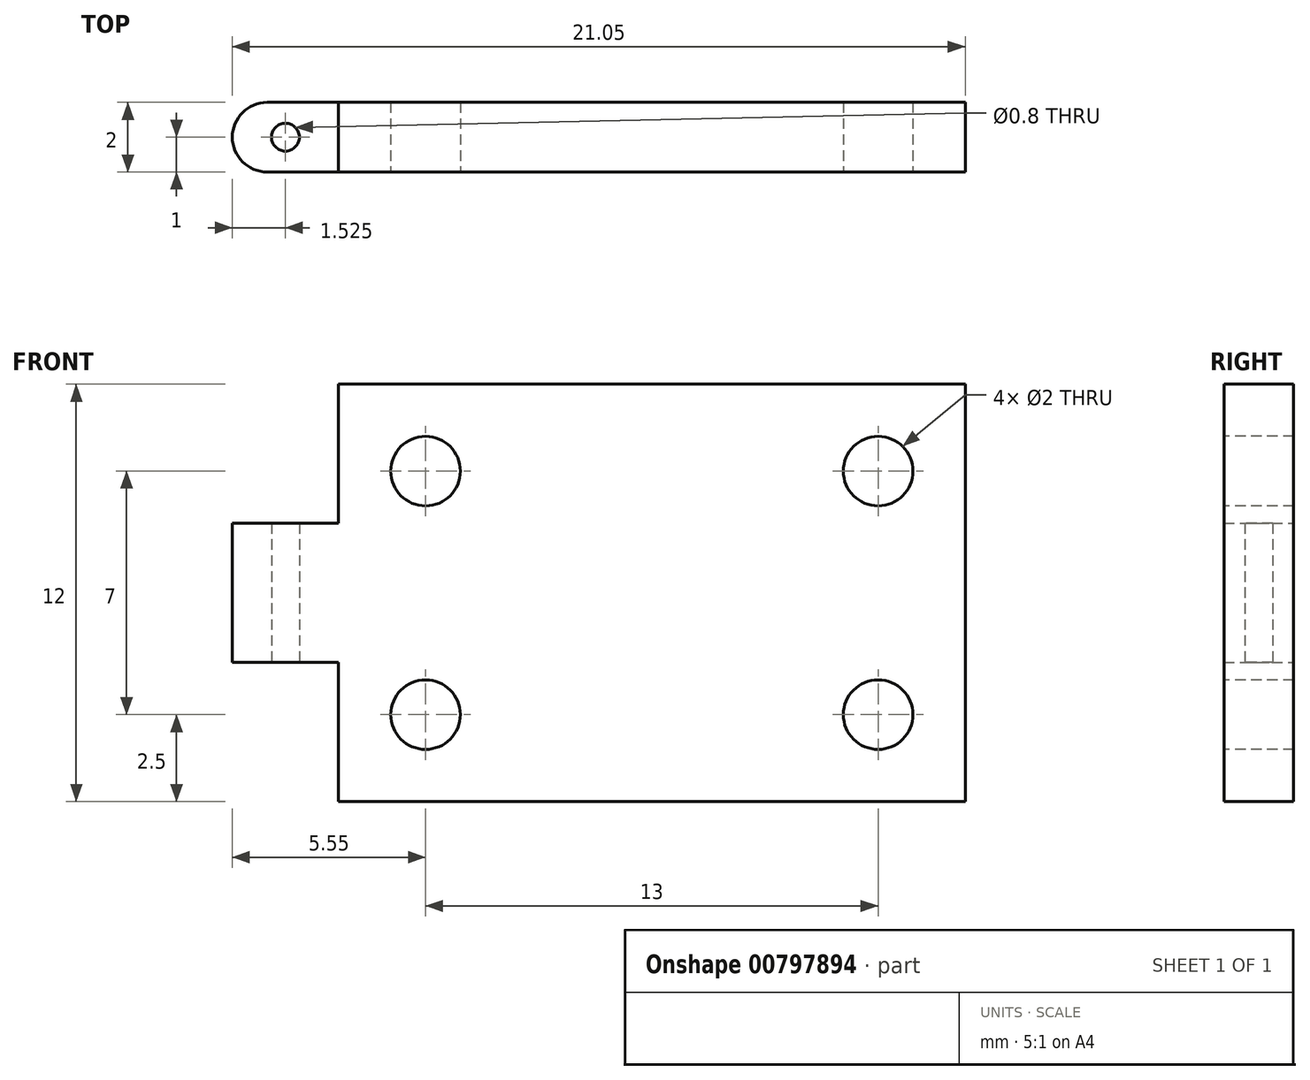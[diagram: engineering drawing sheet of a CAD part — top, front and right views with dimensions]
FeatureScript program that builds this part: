
annotation { "Feature Type Name" : "Feature", "Feature Type Description" : "" }
export const myFeature = defineFeature(function(context is Context, id is Id, definition is map)
    precondition{}
    {
        {
            var Q0;
            Q0=qCreatedBy(makeId("Front.planeOp"),FACE);
            var sketch = newSketch(context, id + "F0", { "sketchPlane" : qUnion([Q0])});
            skLineSegment(sketch, "E0.bottom", {"start": v(9, 6) * mm, "end": v(-9, 6) * mm});
            skLineSegment(sketch, "E0.top", {"start": v(9, -6) * mm, "end": v(-9, -6) * mm});
            skLineSegment(sketch, "E0.left", {"start": v(9, 6) * mm, "end": v(9, -6) * mm});
            skLineSegment(sketch, "E0.right", {"start": v(-9, 6) * mm, "end": v(-9, -6) * mm});
            skPoint(sketch, "E0.middle", {"position": v(0, 0) * mm});
            skLineSegment(sketch, "E1.bottom", {"start": v(-5.95, 2) * mm, "end": v(-12.05, 2) * mm});
            skLineSegment(sketch, "E1.top", {"start": v(-5.95, -2) * mm, "end": v(-12.05, -2) * mm});
            skLineSegment(sketch, "E1.left", {"start": v(-5.95, 2) * mm, "end": v(-5.95, -2) * mm});
            skLineSegment(sketch, "E1.right", {"start": v(-12.05, 2) * mm, "end": v(-12.05, -2) * mm});
            skPoint(sketch, "E1.middle", {"position": v(-9, 0) * mm});
            skSolve(sketch);
        }
        {
            var Q0;
            Q0 = qSketchRegion(id + "F0", true);
            extrude(context, id + "F1", {"entities" : qUnion([Q0]), "depth" : 2 * mm, "offsetDistance" : 25 * mm});
        }
        {
            var Q0;
            Q0=makeQuery(id+"F1.opExtrude","SWEPT_FACE",FACE,{"disambiguationData":[OSD([sQuery(id+"F0.wireOp",EDGE,"E1.top")])]});
            var sketch = newSketch(context, id + "F2", { "sketchPlane" : qUnion([Q0])});
            skLineSegment(sketch, "E2", {"start": v(-12.05, 2) * mm, "end": v(-9, 0) * mm, "construction": true});
            skCircle(sketch, "E3", {"center": v(-10.53, 1) * mm, "radius": 0.4 * mm});
            skSolve(sketch);
        }
        {
            var Q0;
            Q0 = qSketchRegion(id + "F2", true);
            extrude(context, id + "F3", {"entities" : qUnion([Q0]), "operationType" : NewBodyOperationType.REMOVE, "oppositeDirection" : true, "depth" : 25 * mm, "offsetDistance" : 25 * mm});
        }
        {
            var Q0;
            Q0=makeQuery(id+"F1.opExtrude","CAP_FACE",FACE,{"disambiguationData":[OSD([sQuery(id+"F0.wireOp",EDGE,"E0.bottom"),sQuery(id+"F0.wireOp",EDGE,"E0.top"),sQuery(id+"F0.wireOp",EDGE,"E0.left"),sQuery(id+"F0.wireOp",EDGE,"E0.right"),sQuery(id+"F0.wireOp",EDGE,"E1.bottom"),sQuery(id+"F0.wireOp",EDGE,"E1.top"),sQuery(id+"F0.wireOp",EDGE,"E1.right")])],"isStart":false});
            var sketch = newSketch(context, id + "F4", { "sketchPlane" : qUnion([Q0])});
            skLineSegment(sketch, "E4.bottom", {"start": v(6.5, 3.5) * mm, "end": v(-6.5, 3.5) * mm, "construction": true});
            skLineSegment(sketch, "E4.top", {"start": v(6.5, -3.5) * mm, "end": v(-6.5, -3.5) * mm, "construction": true});
            skLineSegment(sketch, "E4.left", {"start": v(6.5, 3.5) * mm, "end": v(6.5, -3.5) * mm, "construction": true});
            skLineSegment(sketch, "E4.right", {"start": v(-6.5, 3.5) * mm, "end": v(-6.5, -3.5) * mm, "construction": true});
            skPoint(sketch, "E4.middle", {"position": v(0, 0) * mm});
            skCircle(sketch, "E5", {"center": v(-6.5, 3.5) * mm, "radius": 1 * mm});
            skCircle(sketch, "E6", {"center": v(6.5, 3.5) * mm, "radius": 1 * mm});
            skCircle(sketch, "E7", {"center": v(6.5, -3.5) * mm, "radius": 1 * mm});
            skCircle(sketch, "E8", {"center": v(-6.5, -3.5) * mm, "radius": 1 * mm});
            skSolve(sketch);
        }
        {
            var Q0;
            Q0 = qSketchRegion(id + "F4", true);
            extrude(context, id + "F5", {"entities" : qUnion([Q0]), "operationType" : NewBodyOperationType.REMOVE, "oppositeDirection" : true, "depth" : 25 * mm, "offsetDistance" : 25 * mm});
        }
        {
            var Q0;
            Q0=makeQuery(id+"F1.opExtrude","CAP_EDGE",EDGE,{"disambiguationData":[OSD([sQuery(id+"F0.wireOp",EDGE,"E1.right")])],"isStart":false});
            var Q1;
            Q1=makeQuery(id+"F1.opExtrude","CAP_EDGE",EDGE,{"disambiguationData":[OSD([sQuery(id+"F0.wireOp",EDGE,"E1.right")])],"isStart":true});
            fillet(context, id + "F6", {"entities" : qUnion([Q0, Q1]), "radius" : 1 * mm, "tangentPropagation" : true, "allowEdgeOverflow" : false});
        }
    });
